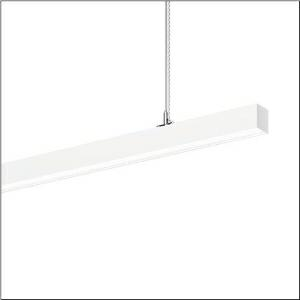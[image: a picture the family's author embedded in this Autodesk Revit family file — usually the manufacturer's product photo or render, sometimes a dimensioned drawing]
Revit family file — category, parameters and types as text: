
# Revit family: silica_r__21_51mx30da34wb_efde
name_source: partatom
category: Lighting Fixtures
units: mm (PartAtom-declared; Revit-internal decimal feet)

## family parameters
Cut with Voids When Loaded = No
Host = Face
Light Source = No
Part Type = Normal
Room Calculation Point = No
Round Connector Dimension = Use Diameter
Shared = No

## types (1)
- --- (1 x LED, 4210 lm, 27.7 W, 3000K)
    Apparent Load = 28 VA
    CIE Flux Codes = 47 79 96 57 100
    Color Rendering = 80
    Color Temperature = 3000K
    Default Elevation = 1800 mm
    Description = Silica® 21, office luminaire, primary optical cover: cover, of PMMA, opal, light emission: direct/indirect distribution, primary light characteristic: symmetric, installation type: suspended mounting, LED, rated luminous flux: 4.210lm, luminous efficacy: 152lm/W, light colour: 830, colour temperature: 3000K, with terminal, 3+2-pole, max. 2.5mm², mains connection: 220..240V, AC, 50/60Hz, rated input power: 27.7W, luminaire housing, of aluminium, traffic white (RAL 9016), length: 1.204mm, width: 53mm, height: 53mm, protection rating (complete): IP20, insulation class (complete): insulation class I (protective earthing), certification: CE, permissible operating ambient temperature: 0..+35°C, standard: EN 50419, packaging unit: 1 piece
    Height = 53 mm
    Lamp = 1 x LED
    Lamp Light Flux = 4210 lm
    Lamp Power = 27.7 W
    Lamp count = 1
    Length = 1204 mm
    Luminous efficacy = 152 lm/W
    Manufacturer = Siteco
    ModVariant = No
    Model = 51MX30DA34WB
    Mounting Place = Ceiling
    Mounting Type = Pendant
    Number of Poles = 1
    OnlyDefault = Yes
    Power Factor = 1
    Product Name = Silica® 21
    Product group = office luminaire | ceiling pendant
    ProductGroupID = 905
    Protection Class = Protection class I
    Protection Degree = IP 20
    RLX_Detail_Level = 1
    RlxData = <blob elided: 21241 chars, md5=1685a7da>
    Socket = socket
    Standby Power = 0 W
    System Light Flux = 4210 lm
    System Power = 28 W
    Type Comments = factory setting: luminous flux: 100 % | dim-lin: 254 | 233 mA
    Type Image = l_1251642.jpg
    URL = http://relux.com
    VarID = @adj_025877
    Voltage = 0 V
    Weight = 0.00 kg
    Width = 53 mm

## geometry (parser evidence)
native form markers: Blend x4, Sweep x13
no freeform markers — native parametric forms only
